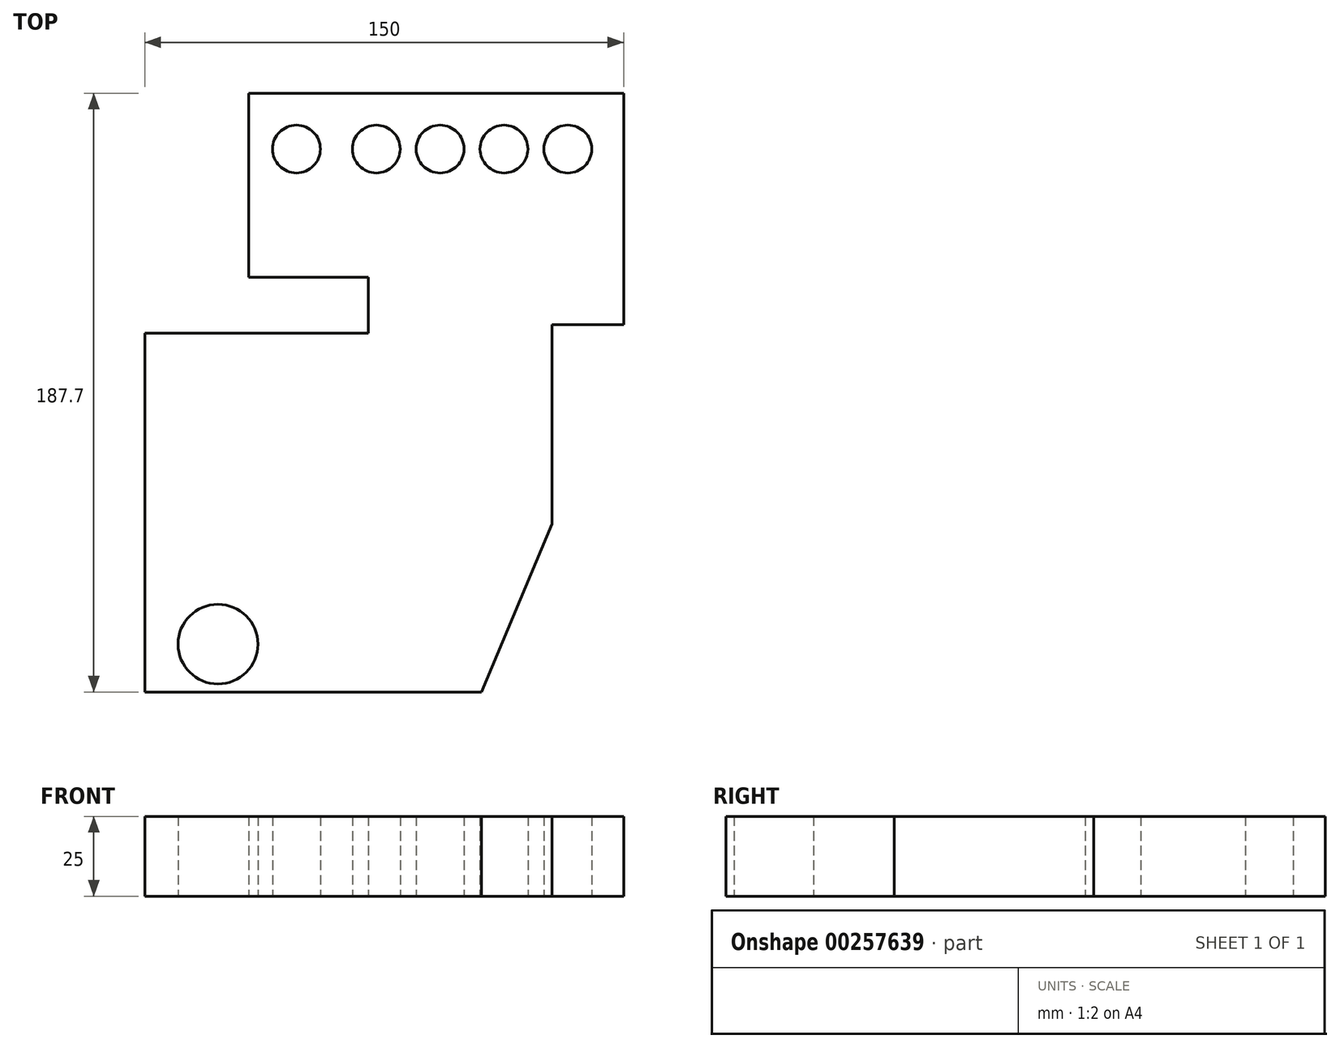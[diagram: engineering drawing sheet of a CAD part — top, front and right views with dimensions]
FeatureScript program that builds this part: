
annotation { "Feature Type Name" : "Feature", "Feature Type Description" : "" }
export const myFeature = defineFeature(function(context is Context, id is Id, definition is map)
    precondition{}
    {
        {
            var Q0;
            Q0=qCreatedBy(makeId("Top.planeOp"),FACE);
            var sketch = newSketch(context, id + "F0", { "sketchPlane" : qUnion([Q0])});
            skLineSegment(sketch, "E0", {"start": v(-37.5, 114.43) * mm, "end": v(80, 114.43) * mm});
            skLineSegment(sketch, "E1", {"start": v(80, 114.43) * mm, "end": v(80, 41.93) * mm});
            skLineSegment(sketch, "E2", {"start": v(80, 41.93) * mm, "end": v(57.5, 41.93) * mm});
            skLineSegment(sketch, "E3", {"start": v(57.5, 41.93) * mm, "end": v(57.5, -20.57) * mm});
            skLineSegment(sketch, "E4", {"start": v(-37.5, 114.43) * mm, "end": v(-37.5, 56.73) * mm});
            skLineSegment(sketch, "E5", {"start": v(-37.5, 56.73) * mm, "end": v(0, 56.73) * mm});
            skLineSegment(sketch, "E6", {"start": v(0, 56.73) * mm, "end": v(0, 39.23) * mm});
            skLineSegment(sketch, "E7", {"start": v(0, 39.23) * mm, "end": v(-70, 39.23) * mm});
            skLineSegment(sketch, "E8", {"start": v(-70, 39.23) * mm, "end": v(-70, -73.27) * mm});
            skLineSegment(sketch, "E9", {"start": v(-50, -73.27) * mm, "end": v(35.42, -73.27) * mm});
            skLineSegment(sketch, "E10", {"start": v(35.42, -73.27) * mm, "end": v(57.5, -20.57) * mm});
            skLineSegment(sketch, "E11", {"start": v(80, 114.43) * mm, "end": v(80, 96.93) * mm});
            skCircle(sketch, "E12", {"center": v(62.5, 96.93) * mm, "radius": 7.5 * mm});
            skCircle(sketch, "E13", {"center": v(42.5, 96.93) * mm, "radius": 7.5 * mm});
            skCircle(sketch, "E14", {"center": v(22.5, 96.93) * mm, "radius": 7.5 * mm});
            skCircle(sketch, "E15", {"center": v(2.5, 96.93) * mm, "radius": 7.5 * mm});
            skCircle(sketch, "E16", {"center": v(-22.5, 96.93) * mm, "radius": 7.5 * mm});
            skLineSegment(sketch, "E17", {"start": v(-70, -73.27) * mm, "end": v(-50, -73.27) * mm});
            skCircle(sketch, "E18", {"center": v(-47.08, -58.27) * mm, "radius": 12.5 * mm});
            skLineSegment(sketch, "E19", {"start": v(-50, -73.27) * mm, "end": v(-25, -73.27) * mm});
            skCircle(sketch, "E20", {"center": v(-22.08, -33.27) * mm, "radius": 12.5 * mm});
            skLineSegment(sketch, "E21", {"start": v(-25, -73.27) * mm, "end": v(0, -73.27) * mm});
            skCircle(sketch, "E22", {"center": v(0, -8.27) * mm, "radius": 12.5 * mm});
            skSolve(sketch);
        }
        {
            var Q0;
            Q0 = qSketchRegion(id + "F0", true);
            var Q1;
            Q1=makeQuery(id+"F0.imprint","IMPRINT",FACE,{"disambiguationData":[TD([[makeQuery(id+"F0.imprint","IMPRINT",EDGE,{"derivedFrom":sQuery(id+"F0.wireOp",EDGE,"E22")}),1.0]])]});
            var Q2;
            Q2=makeQuery(id+"F0.imprint","IMPRINT",FACE,{"disambiguationData":[TD([[makeQuery(id+"F0.imprint","IMPRINT",EDGE,{"derivedFrom":sQuery(id+"F0.wireOp",EDGE,"E20")}),1.0]])]});
            extrude(context, id + "F1", {"entities" : qUnion([Q0, Q1, Q2]), "depth" : 25 * mm});
        }
    });
